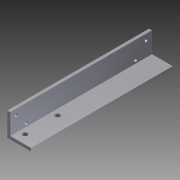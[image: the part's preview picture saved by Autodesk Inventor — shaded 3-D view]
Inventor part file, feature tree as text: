
AUTODESK INVENTOR PART (.ipt)
format: ipt  version: 2012 (Build 160160000, 160)  size: 104,448 bytes
history: native  units: in
note: dims shown in document units (in); Inventor stores cm internally (conversion verified against a paired STEP export)
features: extrude x3, sketch x3
ambient origin geometry x8: Origin, YZ Plane, XZ Plane, XY Plane, X Axis, Y Axis, Z Axis, Center Point
bodies: Solid1 (feature_tree)
feature tree (6):
  extrude  "Extrusion1"  Depth=1.0in
  extrude  "Extrusion4"  Depth=0.125in
  extrude  "Extrusion5"  Depth=0.375in
  sketch  "Sketch1"  dims[d0=1.0in d1=1.0in]
  sketch  "Sketch3"  dims[d2=0.125in d3=0.125in]
  sketch  "Sketch4"  dims[d4=6.0in d5=0.0in d20=0.375in d21=1.375in d22=0.2in d23=0.375in d24=1.0in d25=0.0in d26=0.25in d27=0.75in d28=0.125in d29=0.25in d30=0.6875in d31=1.0in d32=0.0in]
